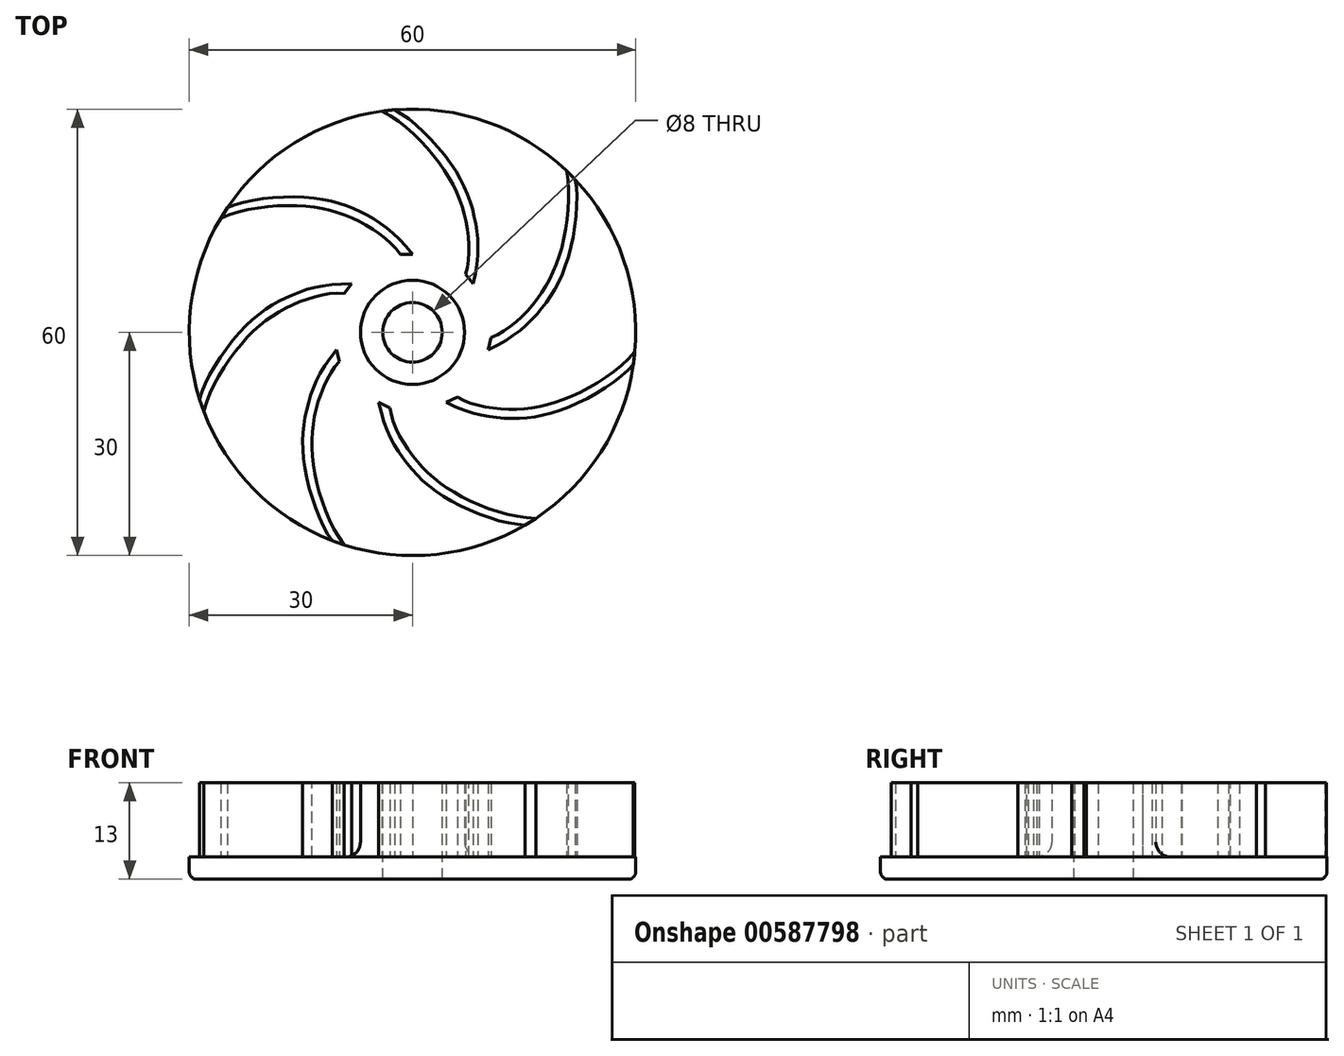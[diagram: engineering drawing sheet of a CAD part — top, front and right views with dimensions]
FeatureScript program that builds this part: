
annotation { "Feature Type Name" : "Feature", "Feature Type Description" : "" }
export const myFeature = defineFeature(function(context is Context, id is Id, definition is map)
    precondition{}
    {
        {
            var Q0;
            Q0=qCreatedBy(makeId("Top.planeOp"),FACE);
            var sketch = newSketch(context, id + "F0", { "sketchPlane" : qUnion([Q0])});
            skCircle(sketch, "E0", {"center": v(0, 0) * mm, "radius": 30 * mm});
            skSolve(sketch);
        }
        {
            var Q0;
            Q0=makeQuery(id+"F0.imprint","IMPRINT",FACE,{"disambiguationData":[TD([[makeQuery(id+"F0.imprint","IMPRINT",EDGE,{"derivedFrom":sQuery(id+"F0.wireOp",EDGE,"E0")}),1.0]])]});
            extrude(context, id + "F1", {"entities" : qUnion([Q0]), "depth" : 3 * mm, "offsetDistance" : 25 * mm});
        }
        {
            var Q0;
            Q0=makeQuery(id+"F1.opExtrude","CAP_FACE",FACE,{"disambiguationData":[OSD([sQuery(id+"F0.wireOp",EDGE,"E0")])],"isStart":false});
            var sketch = newSketch(context, id + "F2", { "sketchPlane" : qUnion([Q0])});
            skFitSpline(sketch, "E1", {"points": [v(0, 10.45) * mm, v(-6.46, 15.93) * mm, v(-13.98, 18.12) * mm, v(-24.88, 16.76) * mm], "startDerivative": vector(-20.73, 26.86) * mm, "endDerivative": vector(-20.88, -9.42) * mm});
            skFitSpline(sketch, "E2", {"points": [v(-1.64, 10.46) * mm, v(-7.1, 14.88) * mm, v(-14.6, 16.96) * mm, v(-25.79, 15.33) * mm], "startDerivative": vector(-11.92, 17.7) * mm, "endDerivative": vector(-26.26, -11.65) * mm});
            skLineSegment(sketch, "E3", {"start": v(-25.79, 15.33) * mm, "end": v(-24.88, 16.76) * mm});
            skLineSegment(sketch, "E4", {"start": v(-1.64, 10.46) * mm, "end": v(0, 10.45) * mm});
            skSolve(sketch);
        }
        {
            var Q0;
            Q0 = qSketchRegion(id + "F2", true);
            extrude(context, id + "F3", {"entities" : qUnion([Q0]), "operationType" : NewBodyOperationType.ADD, "depth" : 10 * mm, "offsetDistance" : 25 * mm});
        }
        {
            var Q0;
            Q0=qCreatedBy(makeId("Front.planeOp"),FACE);
            var sketch = newSketch(context, id + "F4", { "sketchPlane" : qUnion([Q0])});
            skLineSegment(sketch, "E5", {"start": v(0, 0) * mm, "end": v(0, 45.71) * mm, "construction": true});
            skSolve(sketch);
        }
        {
            var Q0;
            Q0=makeQuery(id+"F1.opExtrude","SWEPT_BODY",BODY,{"disambiguationData":[OSD([sQuery(id+"F0.wireOp",EDGE,"E0")])]});
            var Q1;
            Q1=sQuery(id+"F4.wireOp",EDGE,"E5");
            circularPattern(context, id + "F5", {"entities" : qUnion([Q0]), "axis" : qUnion([Q1]), "angle" : 360 * degree, "instanceCount" : 7, "equalSpace" : true});
        }
        {
            var Q0;
            Q0=makeQuery(id+"F5.opPattern","COPY",FACE,{"derivedFrom":makeQuery(id+"F1.opExtrude","CAP_FACE",FACE,{"disambiguationData":[OSD([sQuery(id+"F0.wireOp",EDGE,"E0")])],"isStart":false}),"instanceName":"1"});
            var sketch = newSketch(context, id + "F6", { "sketchPlane" : qUnion([Q0])});
            skCircle(sketch, "E6", {"center": v(0, 0) * mm, "radius": 7 * mm});
            skSolve(sketch);
        }
        {
            var Q0;
            Q0 = qSketchRegion(id + "F6", true);
            var Q1;
            Q1=sQuery(id+"F6.wireOp",EDGE,"E6");
            extrude(context, id + "F7", {"entities" : qUnion([Q0]), "operationType" : NewBodyOperationType.ADD, "surfaceEntities" : qUnion([Q1]), "depth" : 10 * mm, "offsetDistance" : 25 * mm});
        }
        {
            var Q0;
            Q0=makeQuery(id+"F7.opExtrude","CAP_FACE",FACE,{"disambiguationData":[OSD([sQuery(id+"F6.wireOp",EDGE,"E6")])],"isStart":false});
            var sketch = newSketch(context, id + "F8", { "sketchPlane" : qUnion([Q0])});
            skCircle(sketch, "E7", {"center": v(0, 0) * mm, "radius": 4 * mm});
            skSolve(sketch);
        }
        {
            var Q0;
            Q0=makeQuery(id+"F8.imprint","IMPRINT",FACE,{"disambiguationData":[TD([[makeQuery(id+"F8.imprint","IMPRINT",EDGE,{"derivedFrom":sQuery(id+"F8.wireOp",EDGE,"E7")}),1.0]])]});
            extrude(context, id + "F9", {"entities" : qUnion([Q0]), "operationType" : NewBodyOperationType.REMOVE, "endBound" : BoundingType.THROUGH_ALL, "oppositeDirection" : true, "depth" : 25 * mm, "offsetDistance" : 25 * mm});
        }
        {
            var Q0;
            Q0=makeQuery(id+"F1.opExtrude","CAP_EDGE",EDGE,{"disambiguationData":[OSD([sQuery(id+"F0.wireOp",EDGE,"E0")])],"isStart":true});
            fillet(context, id + "F10", {"entities" : qUnion([Q0]), "radius" : 1 * mm, "tangentPropagation" : true, "allowEdgeOverflow" : false});
        }
        {
            var Q0;
            {var subQ0=sQuery(id+"F0.wireOp",EDGE,"E0");var subQ1=makeQuery(id+"F1.opExtrude","CAP_FACE",FACE,{"disambiguationData":[OSD([subQ0])],"isStart":false});var subQ2=makeQuery(id+"F3.boolean.opBoolean","SPLIT",FACE,{"disambiguationData":[TD([makeQuery(id+"F1.opExtrude","SWEPT_FACE",FACE,{"disambiguationData":[OSD([subQ0])]}),subQ1,makeQuery(id+"F3.opExtrude","SWEPT_FACE",FACE,{"disambiguationData":[OSD([sQuery(id+"F2.wireOp",EDGE,"E1")])]}),makeQuery(id+"F3.opExtrude","SWEPT_FACE",FACE,{"disambiguationData":[OSD([sQuery(id+"F2.wireOp",EDGE,"E2")])]}),makeQuery(id+"F3.opExtrude","SWEPT_FACE",FACE,{"disambiguationData":[OSD([sQuery(id+"F2.wireOp",EDGE,"E3")])]}),makeQuery(id+"F3.opExtrude","SWEPT_FACE",FACE,{"disambiguationData":[OSD([sQuery(id+"F2.wireOp",EDGE,"E4")])]})])],"derivedFrom":subQ1});Q0=makeQuery(id+"F7.boolean.opBoolean","INTERSECT",EDGE,{"derivedFrom":[subQ2,makeQuery(id+"F5.opPattern","COPY",FACE,{"derivedFrom":subQ2,"instanceName":"1"}),makeQuery(id+"F5.opPattern","COPY",FACE,{"derivedFrom":subQ2,"instanceName":"2"}),makeQuery(id+"F5.opPattern","COPY",FACE,{"derivedFrom":subQ2,"instanceName":"3"}),makeQuery(id+"F5.opPattern","COPY",FACE,{"derivedFrom":subQ2,"instanceName":"4"}),makeQuery(id+"F5.opPattern","COPY",FACE,{"derivedFrom":subQ2,"instanceName":"5"}),makeQuery(id+"F5.opPattern","COPY",FACE,{"derivedFrom":subQ2,"instanceName":"6"})]});}
            fillet(context, id + "F11", {"entities" : qUnion([Q0]), "radius" : 2 * mm, "tangentPropagation" : true, "allowEdgeOverflow" : false});
        }
    });
